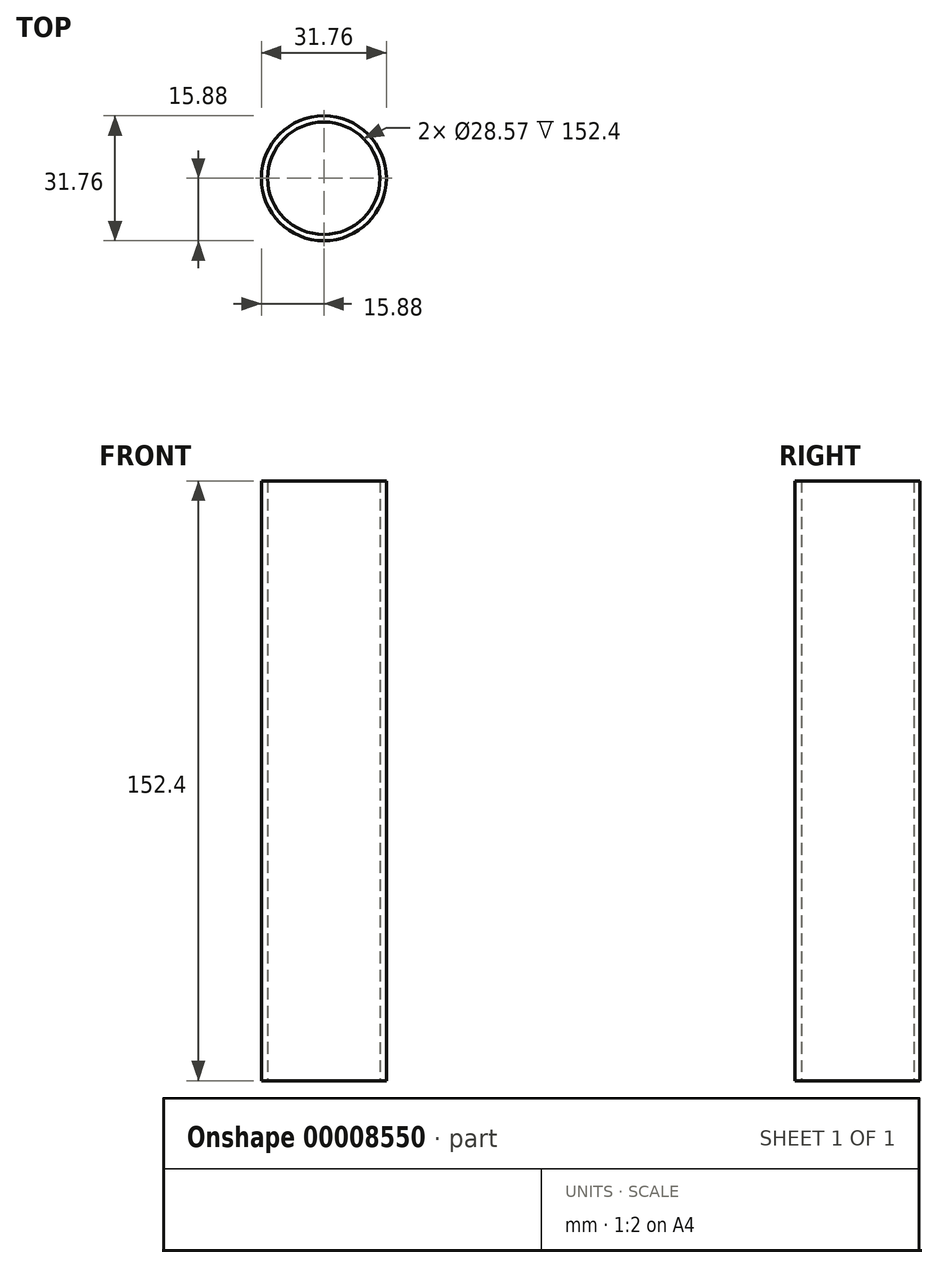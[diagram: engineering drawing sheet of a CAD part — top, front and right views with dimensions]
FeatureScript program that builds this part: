
annotation { "Feature Type Name" : "Feature", "Feature Type Description" : "" }
export const myFeature = defineFeature(function(context is Context, id is Id, definition is map)
    precondition{}
    {
        {
            var Q0;
            Q0=qCreatedBy(makeId("Top.planeOp"),FACE);
            var sketch = newSketch(context, id + "F0", { "sketchPlane" : qUnion([Q0])});
            skCircle(sketch, "E0", {"center": v(0, 0) * mm, "radius": 15.88 * mm});
            skCircle(sketch, "E1", {"center": v(0, 0) * mm, "radius": 14.29 * mm});
            skSolve(sketch);
        }
        {
            var Q0;
            Q0 = qSketchRegion(id + "F0", true);
            extrude(context, id + "F1", {"entities" : qUnion([Q0]), "depth" : 152.4 * mm});
        }
    });
